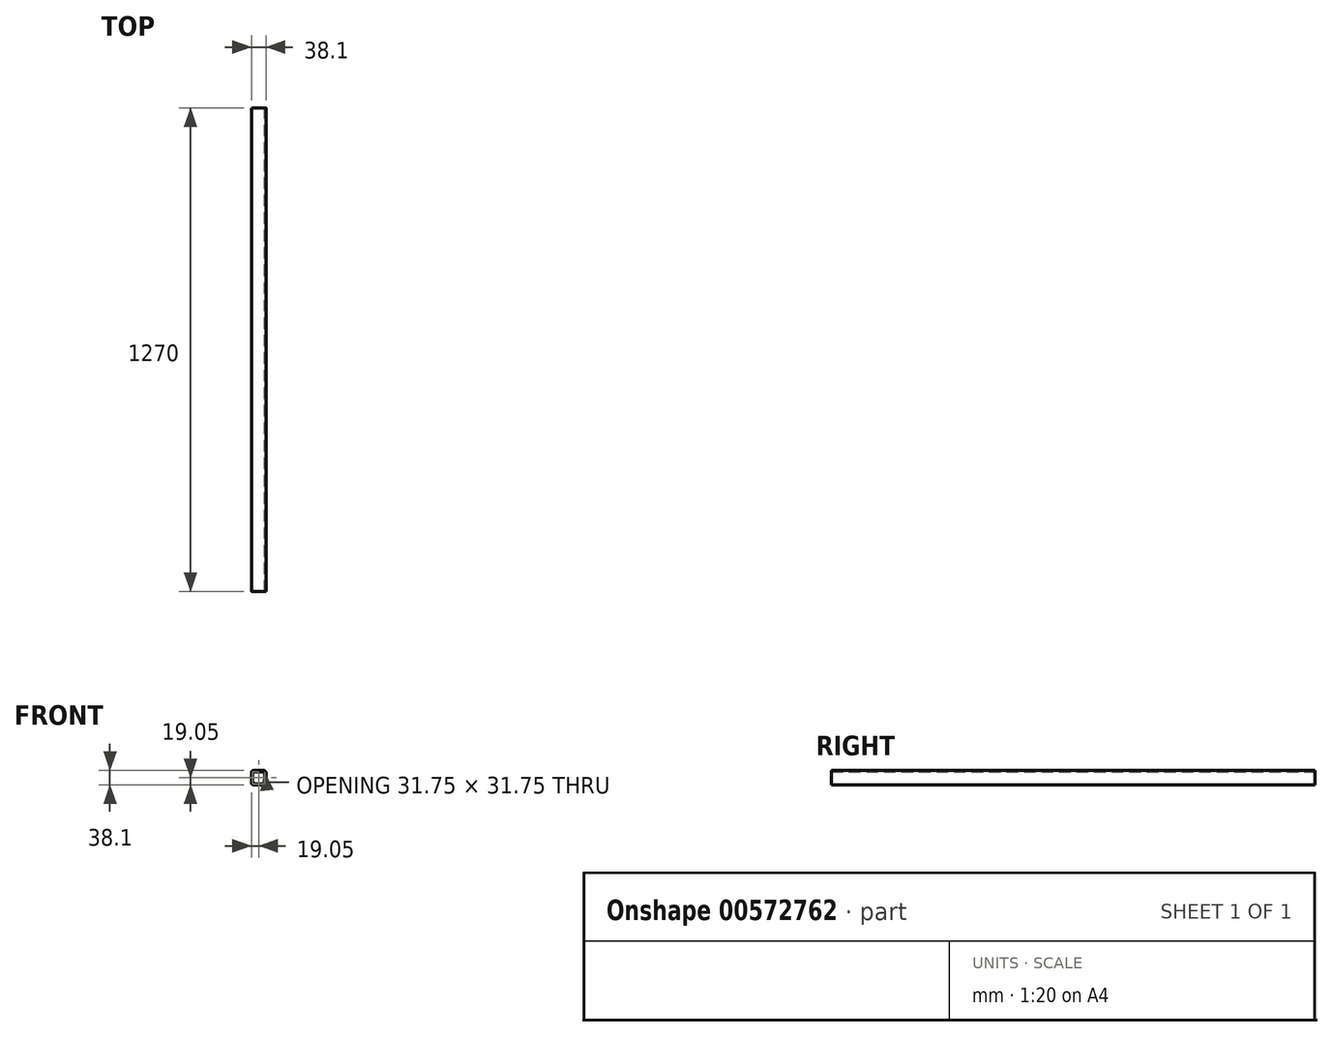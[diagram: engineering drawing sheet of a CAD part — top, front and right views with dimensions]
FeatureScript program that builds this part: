
annotation { "Feature Type Name" : "Feature", "Feature Type Description" : "" }
export const myFeature = defineFeature(function(context is Context, id is Id, definition is map)
    precondition{}
    {
        {
            var Q0;
            Q0=qCreatedBy(makeId("Front.planeOp"),FACE);
            var sketch = newSketch(context, id + "F0", { "sketchPlane" : qUnion([Q0])});
            skLineSegment(sketch, "E0.bottom", {"start": v(6.35, 0) * mm, "end": v(31.75, 0) * mm});
            skLineSegment(sketch, "E0.top", {"start": v(6.35, 38.1) * mm, "end": v(31.75, 38.1) * mm});
            skLineSegment(sketch, "E0.left", {"start": v(0, 6.35) * mm, "end": v(0, 31.75) * mm});
            skLineSegment(sketch, "E0.right", {"start": v(38.1, 6.35) * mm, "end": v(38.1, 31.75) * mm});
            skLineSegment(sketch, "E1.bottom", {"start": v(9.52, 3.18) * mm, "end": v(28.57, 3.18) * mm});
            skLineSegment(sketch, "E1.top", {"start": v(9.52, 34.92) * mm, "end": v(28.57, 34.92) * mm});
            skLineSegment(sketch, "E1.left", {"start": v(3.17, 9.52) * mm, "end": v(3.17, 28.57) * mm});
            skLineSegment(sketch, "E1.right", {"start": v(34.92, 9.53) * mm, "end": v(34.92, 28.57) * mm});
            skPoint(sketch, "E2.visualSharp", {"position": v(0, 38.1) * mm});
            skArc(sketch, "E2.filletArc", {"start": v(6.35, 38.1) * mm, "mid": v(1.86, 36.24) * mm, "end": v(0, 31.75) * mm});
            skPoint(sketch, "E3.visualSharp", {"position": v(34.92, 34.92) * mm});
            skArc(sketch, "E3.filletArc", {"start": v(34.92, 28.57) * mm, "mid": v(33.07, 33.07) * mm, "end": v(28.57, 34.92) * mm});
            skPoint(sketch, "E4.visualSharp", {"position": v(3.17, 34.92) * mm});
            skArc(sketch, "E4.filletArc", {"start": v(9.52, 34.92) * mm, "mid": v(5.03, 33.07) * mm, "end": v(3.17, 28.57) * mm});
            skPoint(sketch, "E5.visualSharp", {"position": v(38.1, 38.1) * mm});
            skArc(sketch, "E5.filletArc", {"start": v(38.1, 31.75) * mm, "mid": v(36.24, 36.24) * mm, "end": v(31.75, 38.1) * mm});
            skPoint(sketch, "E6.visualSharp", {"position": v(38.1, 0) * mm});
            skArc(sketch, "E6.filletArc", {"start": v(31.75, 0) * mm, "mid": v(36.24, 1.86) * mm, "end": v(38.1, 6.35) * mm});
            skPoint(sketch, "E7.visualSharp", {"position": v(0, 0) * mm});
            skArc(sketch, "E7.filletArc", {"start": v(0, 6.35) * mm, "mid": v(1.86, 1.86) * mm, "end": v(6.35, 0) * mm});
            skPoint(sketch, "E8.visualSharp", {"position": v(3.17, 3.18) * mm});
            skArc(sketch, "E8.filletArc", {"start": v(3.17, 9.52) * mm, "mid": v(5.03, 5.03) * mm, "end": v(9.52, 3.18) * mm});
            skPoint(sketch, "E9.visualSharp", {"position": v(34.92, 3.18) * mm});
            skArc(sketch, "E9.filletArc", {"start": v(28.57, 3.18) * mm, "mid": v(33.07, 5.03) * mm, "end": v(34.92, 9.53) * mm});
            skSolve(sketch);
        }
        {
            var Q0;
            Q0=qSketchRegion(id+"F0",true);
            extrude(context, id + "F1", {"entities" : qUnion([Q0]), "depth" : 1270 * mm, "offsetDistance" : 25.4 * mm});
        }
    });
